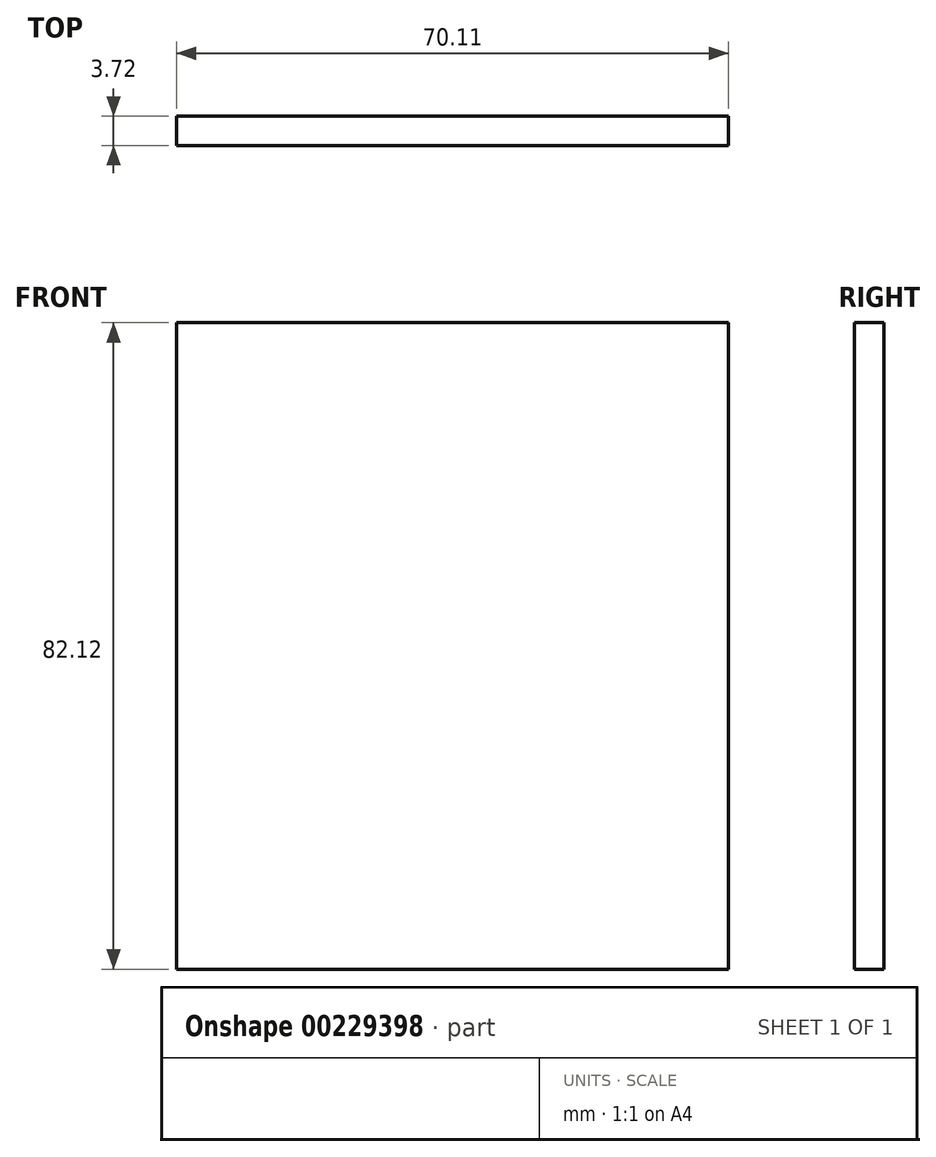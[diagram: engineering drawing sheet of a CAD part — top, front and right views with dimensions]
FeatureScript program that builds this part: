
annotation { "Feature Type Name" : "Feature", "Feature Type Description" : "" }
export const myFeature = defineFeature(function(context is Context, id is Id, definition is map)
    precondition{}
    {
        {
            var Q0;
            Q0=qCreatedBy(makeId("Front.planeOp"),FACE);
            var sketch = newSketch(context, id + "F0", { "sketchPlane" : qUnion([Q0])});
            skLineSegment(sketch, "E0.bottom", {"start": v(41.1, 41.1) * mm, "end": v(-41.1, 41.1) * mm});
            skLineSegment(sketch, "E0.top", {"start": v(41.1, -41.1) * mm, "end": v(-41.1, -41.1) * mm});
            skLineSegment(sketch, "E0.left", {"start": v(41.1, 41.1) * mm, "end": v(41.1, -41.1) * mm});
            skLineSegment(sketch, "E0.right", {"start": v(-41.1, 41.1) * mm, "end": v(-41.1, -41.1) * mm});
            skPoint(sketch, "E0.middle", {"position": v(0, 0) * mm});
            skSolve(sketch);
        }
        {
            var Q0;
            Q0=qCreatedBy(makeId("Front.planeOp"),FACE);
            var sketch = newSketch(context, id + "F1", { "sketchPlane" : qUnion([Q0])});
            skLineSegment(sketch, "E1.bottom", {"start": v(-41.22, 41.06) * mm, "end": v(-111.33, 41.06) * mm});
            skLineSegment(sketch, "E1.top", {"start": v(-41.22, -41.06) * mm, "end": v(-111.33, -41.06) * mm});
            skLineSegment(sketch, "E1.left", {"start": v(-41.22, 41.06) * mm, "end": v(-41.22, -41.06) * mm});
            skLineSegment(sketch, "E1.right", {"start": v(-111.33, 41.06) * mm, "end": v(-111.33, -41.06) * mm});
            skPoint(sketch, "E1.middle", {"position": v(-76.28, 0) * mm});
            skLineSegment(sketch, "E2.bottom", {"start": v(40.9, 41.06) * mm, "end": v(111, 41.06) * mm});
            skLineSegment(sketch, "E2.top", {"start": v(40.9, -41.06) * mm, "end": v(111, -41.06) * mm});
            skLineSegment(sketch, "E2.left", {"start": v(40.9, 41.06) * mm, "end": v(40.9, -41.06) * mm});
            skLineSegment(sketch, "E2.right", {"start": v(111, 41.06) * mm, "end": v(111, -41.06) * mm});
            skPoint(sketch, "E2.middle", {"position": v(75.95, 0) * mm});
            skSolve(sketch);
        }
        {
            var Q0;
            Q0=makeQuery(id+"F0.imprint","IMPRINT",FACE,{"disambiguationData":[TD([[makeQuery(id+"F0.imprint","IMPRINT",EDGE,{"derivedFrom":sQuery(id+"F0.wireOp",EDGE,"E0.bottom")}),1.0]])]});
            extrude(context, id + "F2", {"entities" : qUnion([Q0]), "depth" : 3.72 * mm});
        }
        {
            var Q0;
            Q0=makeQuery(id+"F1.imprint","IMPRINT",FACE,{"disambiguationData":[TD([[makeQuery(id+"F1.imprint","IMPRINT",EDGE,{"derivedFrom":sQuery(id+"F1.wireOp",EDGE,"E1.bottom")}),1.0]])]});
            var Q1;
            Q1=makeQuery(id+"F1.imprint","IMPRINT",FACE,{"disambiguationData":[TD([[makeQuery(id+"F1.imprint","IMPRINT",EDGE,{"derivedFrom":sQuery(id+"F1.wireOp",EDGE,"E2.bottom")}),-1.0]])]});
            extrude(context, id + "F3", {"entities" : qUnion([Q0, Q1]), "operationType" : NewBodyOperationType.ADD, "oppositeDirection" : true, "depth" : 3.72 * mm});
        }
        {
            var Q0;
            Q0=makeQuery(id+"F3.opExtrude","CAP_FACE",FACE,{"disambiguationData":[OSD([sQuery(id+"F1.wireOp",EDGE,"E1.bottom"),sQuery(id+"F1.wireOp",EDGE,"E1.top"),sQuery(id+"F1.wireOp",EDGE,"E1.left"),sQuery(id+"F1.wireOp",EDGE,"E1.right")])],"isStart":true});
            var sketch = newSketch(context, id + "F4", { "sketchPlane" : qUnion([Q0])});
            skCircle(sketch, "E3", {"center": v(-103.71, 33.44) * mm, "radius": 0.84 * mm});
            skCircle(sketch, "E4", {"center": v(-103.71, -33.44) * mm, "radius": 0.82 * mm});
            skCircle(sketch, "E5", {"center": v(103.39, 33.44) * mm, "radius": 0.94 * mm});
            skCircle(sketch, "E6", {"center": v(103.39, -33.44) * mm, "radius": 1.35 * mm});
            skCircle(sketch, "E7", {"center": v(-103.71, -33.44) * mm, "radius": 1.02 * mm});
            skSolve(sketch);
        }
        {
            var Q0;
            Q0=makeQuery(id+"F4.imprint","IMPRINT",FACE,{"disambiguationData":[TD([[makeQuery(id+"F4.imprint","IMPRINT",EDGE,{"derivedFrom":sQuery(id+"F4.wireOp",EDGE,"E5")}),1.0]])]});
            var Q1;
            Q1=makeQuery(id+"F4.imprint","IMPRINT",FACE,{"disambiguationData":[TD([[makeQuery(id+"F4.imprint","IMPRINT",EDGE,{"derivedFrom":sQuery(id+"F4.wireOp",EDGE,"E6")}),1.0]])]});
            var Q2;
            Q2=makeQuery(id+"F2.opExtrude","CAP_FACE",FACE,{"disambiguationData":[OSD([sQuery(id+"F0.wireOp",EDGE,"E0.bottom"),sQuery(id+"F0.wireOp",EDGE,"E0.top"),sQuery(id+"F0.wireOp",EDGE,"E0.left"),sQuery(id+"F0.wireOp",EDGE,"E0.right")])],"isStart":false});
            var Q3;
            Q3=makeQuery(id+"F3.opExtrude","CAP_FACE",FACE,{"disambiguationData":[OSD([sQuery(id+"F1.wireOp",EDGE,"E2.bottom"),sQuery(id+"F1.wireOp",EDGE,"E2.top"),sQuery(id+"F1.wireOp",EDGE,"E2.left"),sQuery(id+"F1.wireOp",EDGE,"E2.right")])],"isStart":true});
            extrude(context, id + "F5", {"entities" : qUnion([Q0, Q1, Q2, Q3]), "operationType" : NewBodyOperationType.REMOVE, "endBound" : BoundingType.THROUGH_ALL, "oppositeDirection" : true, "depth" : 25.4 * mm});
        }
    });
